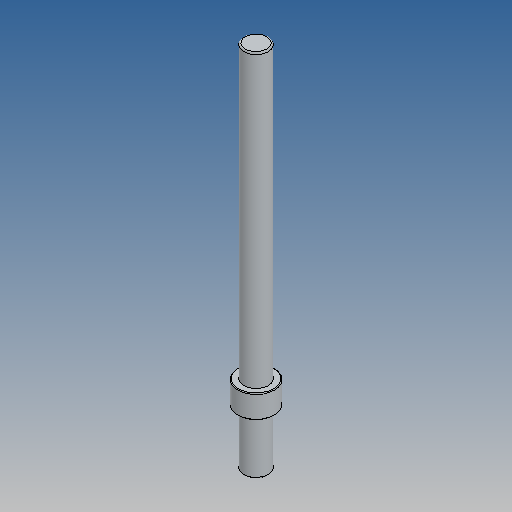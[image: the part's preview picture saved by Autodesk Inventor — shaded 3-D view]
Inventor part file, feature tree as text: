
AUTODESK INVENTOR PART (.ipt)
format: ipt  version: 2025 (Build 290162010, 162A)  size: 124,928 bytes
history: native  units: in
note: dims shown in document units (in); Inventor stores cm internally (conversion verified against a paired STEP export)
features: revolve x1, fillet x1, sketch x1
ambient origin geometry x8: Origin, YZ Plane, XZ Plane, XY Plane, X Axis, Y Axis, Z Axis, Center Point
bodies: Solid1 (feature_tree)
feature tree (3):
  revolve  "Revolution1"  [1 undecoded]
  fillet  "Fillet1"  Radius=0.1181in
  sketch  "Sketch1"  dims[d1=1.8898in d2=0.126in d3=0.1181in d4=0.189in d5=0.2835in d6=90.0deg d7=0.0039in d8=0.0079in]
note: 1 required parameter value undecoded (feature->parameter linkage not recoverable at this tier; creation-order binding heuristic only, values carry confidence <= 0.55)
